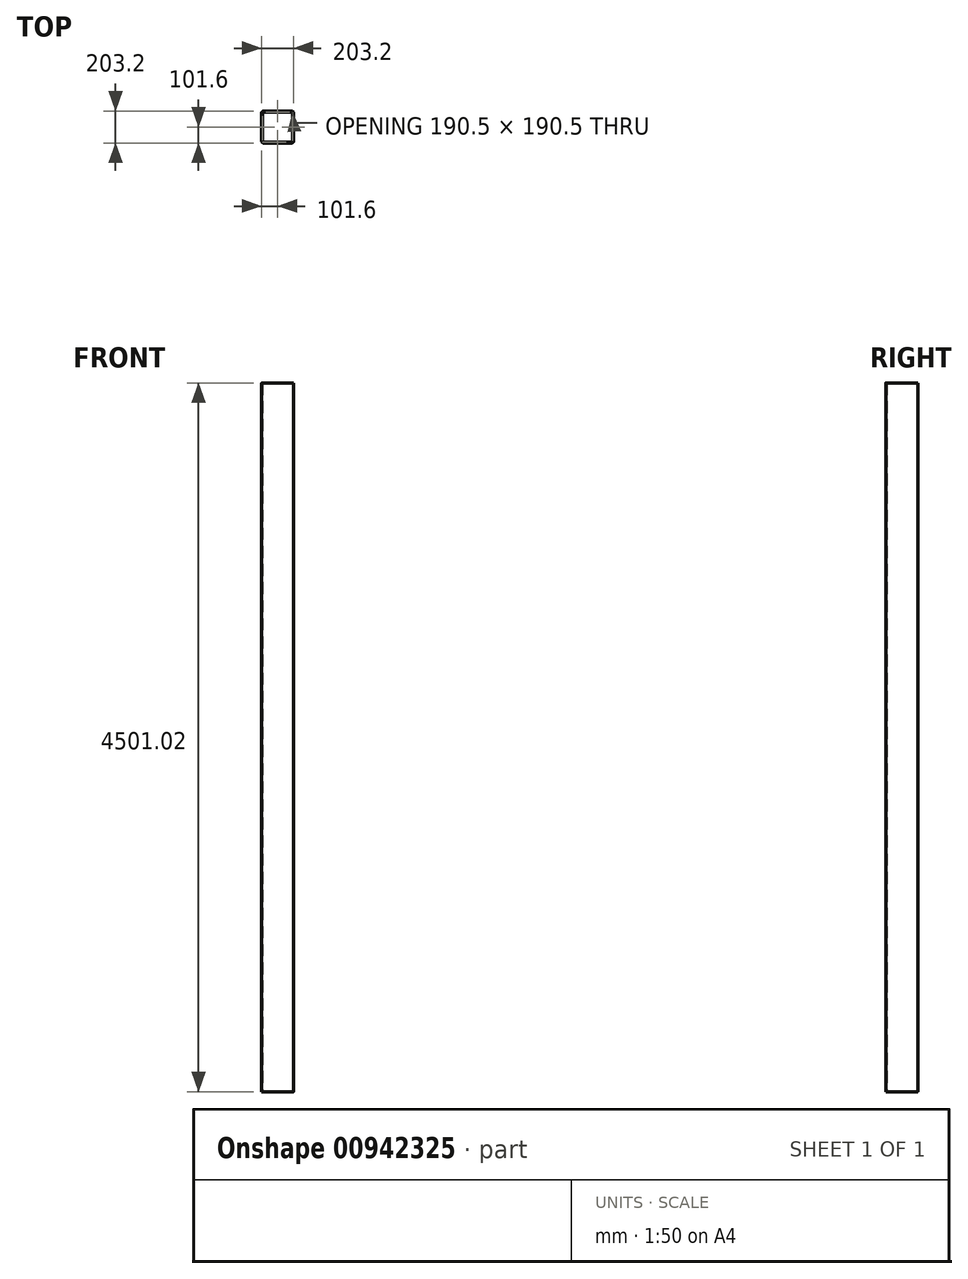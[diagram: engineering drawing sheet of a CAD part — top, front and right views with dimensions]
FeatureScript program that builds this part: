
annotation { "Feature Type Name" : "Feature", "Feature Type Description" : "" }
export const myFeature = defineFeature(function(context is Context, id is Id, definition is map)
    precondition{}
    {
        {
            assignVariable(context, id + "F0", {"name" : "r", "anyValue" : 80 * mm});
        }
        {
            assignVariable(context, id + "F1", {"name" : "E", "anyValue" : 29500000 * pound / mm ^ 2});
        }
        {
            assignVariable(context, id + "F2", {"name" : "Fy", "anyValue" : 46000 * pound / mm ^ 2});
        }
        {
            assignVariable(context, id + "F3", {"name" : "Cc", "anyValue" : sqrt(2 * PI ^ 2 * getVariable(context, 'E') / getVariable(context, 'Fy'))});
        }
        {
            assignVariable(context, id + "F4", {"name" : "K", "anyValue" : 2});
        }
        {
            assignVariable(context, id + "F5", {"name" : "z", "anyValue" : 1});
        }
        {
            assignVariable(context, id + "F6", {"name" : "length", "anyValue" : getVariable(context, 'z') * getVariable(context, 'Cc') * getVariable(context, 'r') / getVariable(context, 'K')});
        }
        {
            var Q0;
            Q0=qCreatedBy(makeId("Top.planeOp"),FACE);
            var sketch = newSketch(context, id + "F7", { "sketchPlane" : qUnion([Q0])});
            skLineSegment(sketch, "E0.bottom", {"start": v(-88.66, 101.6) * mm, "end": v(88.66, 101.6) * mm});
            skLineSegment(sketch, "E0.top", {"start": v(-88.66, -101.6) * mm, "end": v(88.66, -101.6) * mm});
            skLineSegment(sketch, "E0.left", {"start": v(-101.6, 88.66) * mm, "end": v(-101.6, -88.66) * mm});
            skLineSegment(sketch, "E0.right", {"start": v(101.6, 88.66) * mm, "end": v(101.6, -88.66) * mm});
            skPoint(sketch, "E1.visualSharp", {"position": v(-101.6, 101.6) * mm});
            skArc(sketch, "E1.filletArc", {"start": v(-88.66, 101.6) * mm, "mid": v(-97.81, 97.81) * mm, "end": v(-101.6, 88.66) * mm});
            skPoint(sketch, "E2.visualSharp", {"position": v(101.6, 101.6) * mm});
            skArc(sketch, "E2.filletArc", {"start": v(101.6, 88.66) * mm, "mid": v(97.81, 97.81) * mm, "end": v(88.66, 101.6) * mm});
            skPoint(sketch, "E3.visualSharp", {"position": v(101.6, -101.6) * mm});
            skArc(sketch, "E3.filletArc", {"start": v(88.66, -101.6) * mm, "mid": v(97.81, -97.81) * mm, "end": v(101.6, -88.66) * mm});
            skPoint(sketch, "E4.visualSharp", {"position": v(-101.6, -101.6) * mm});
            skArc(sketch, "E4.filletArc", {"start": v(-101.6, -88.66) * mm, "mid": v(-97.81, -97.81) * mm, "end": v(-88.66, -101.6) * mm});
            skLineSegment(sketch, "E5.0", {"start": v(-88.66, 95.25) * mm, "end": v(88.66, 95.25) * mm});
            skArc(sketch, "E5.1", {"start": v(95.25, 88.66) * mm, "mid": v(93.32, 93.32) * mm, "end": v(88.66, 95.25) * mm});
            skArc(sketch, "E5.2", {"start": v(-88.66, 95.25) * mm, "mid": v(-93.32, 93.32) * mm, "end": v(-95.25, 88.66) * mm});
            skLineSegment(sketch, "E5.3", {"start": v(95.25, 88.66) * mm, "end": v(95.25, -88.66) * mm});
            skLineSegment(sketch, "E5.4", {"start": v(-95.25, 88.66) * mm, "end": v(-95.25, -88.66) * mm});
            skArc(sketch, "E5.5", {"start": v(-95.25, -88.66) * mm, "mid": v(-93.32, -93.32) * mm, "end": v(-88.66, -95.25) * mm});
            skLineSegment(sketch, "E5.6", {"start": v(-88.66, -95.25) * mm, "end": v(88.66, -95.25) * mm});
            skArc(sketch, "E5.7", {"start": v(88.66, -95.25) * mm, "mid": v(93.32, -93.32) * mm, "end": v(95.25, -88.66) * mm});
            skLineSegment(sketch, "E6", {"start": v(101.6, 101.6) * mm, "end": v(-101.6, -101.6) * mm, "construction": true});
            skPoint(sketch, "E7", {"position": v(0, 0) * mm});
            skSolve(sketch);
        }
        {
            var Q0;
            Q0=makeQuery(id+"F7.imprint","IMPRINT",FACE,{"disambiguationData":[TD([[makeQuery(id+"F7.imprint","IMPRINT",EDGE,{"derivedFrom":sQuery(id+"F7.wireOp",EDGE,"E0.bottom")}),-1.0]])]});
            var Q1;
            Q1 = qConstructionFilter(qBodyType(qCreatedBy(id + "F7" ,EDGE), BodyType.WIRE), ConstructionObject.NO);
            extrude(context, id + "F8", {"entities" : qUnion([Q0]), "surfaceEntities" : qUnion([Q1]), "depth" : getVariable(context, 'length'), "offsetDistance" : 25.4 * mm});
        }
    });
